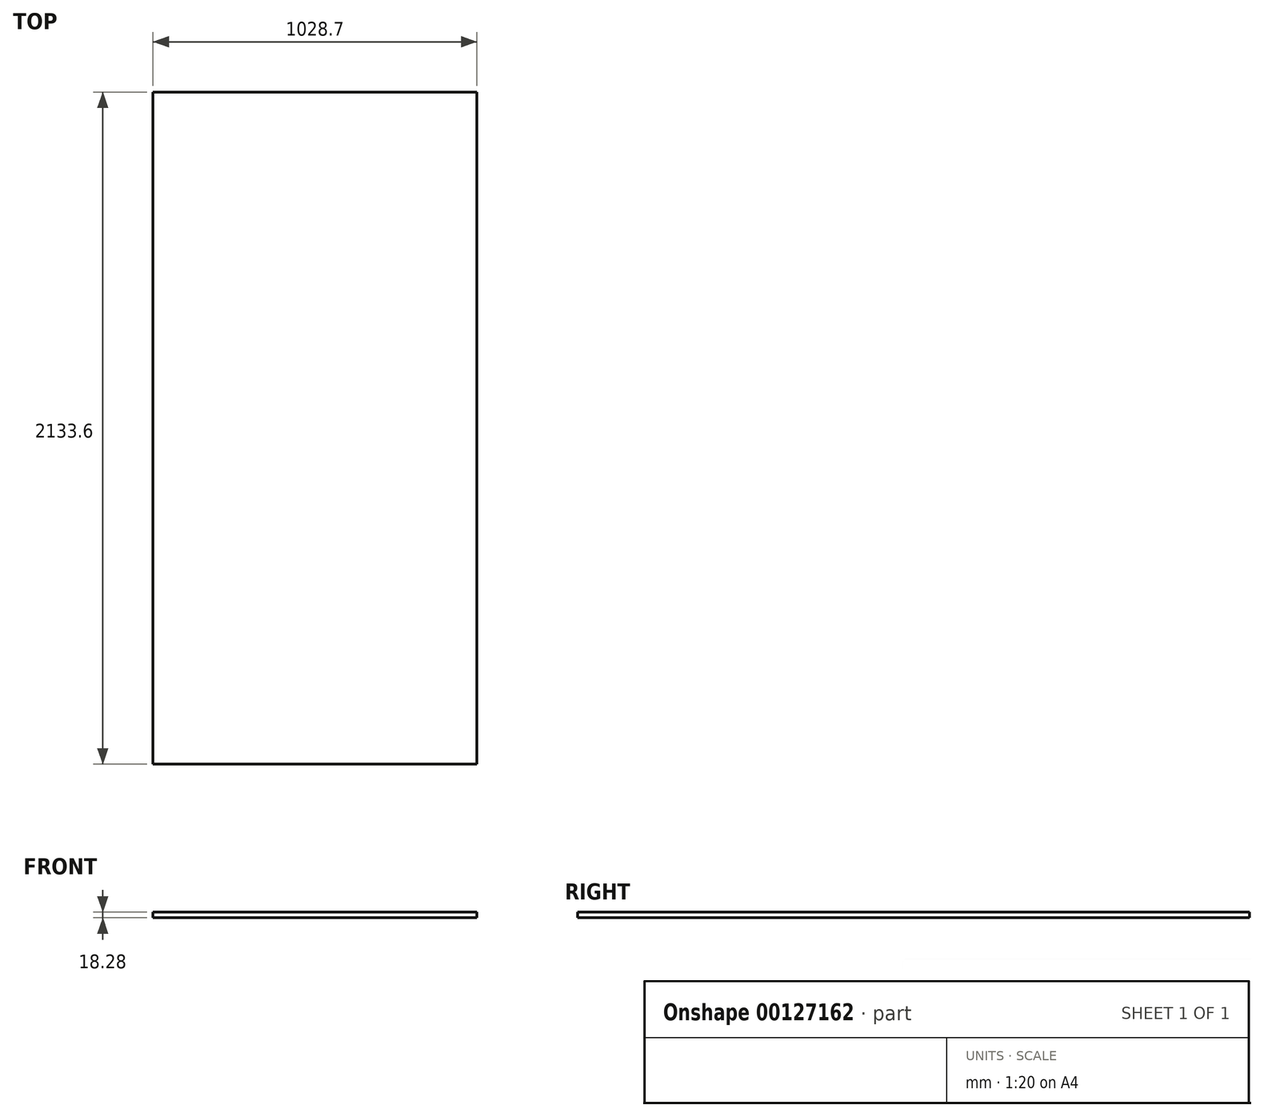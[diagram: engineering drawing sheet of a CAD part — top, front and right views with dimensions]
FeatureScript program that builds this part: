
annotation { "Feature Type Name" : "Feature", "Feature Type Description" : "" }
export const myFeature = defineFeature(function(context is Context, id is Id, definition is map)
    precondition{}
    {
        {
            var Q0;
            Q0=qCreatedBy(makeId("Front.planeOp"),FACE);
            var sketch = newSketch(context, id + "F0", { "sketchPlane" : qUnion([Q0])});
            skLineSegment(sketch, "E0.bottom", {"start": v(514.35, -9.14) * mm, "end": v(-514.35, -9.14) * mm});
            skLineSegment(sketch, "E0.top", {"start": v(514.35, 9.14) * mm, "end": v(-514.35, 9.14) * mm});
            skLineSegment(sketch, "E0.left", {"start": v(514.35, -9.14) * mm, "end": v(514.35, 9.14) * mm});
            skLineSegment(sketch, "E0.right", {"start": v(-514.35, -9.14) * mm, "end": v(-514.35, 9.14) * mm});
            skPoint(sketch, "E0.middle", {"position": v(0, 0) * mm});
            skSolve(sketch);
        }
        {
            var Q0;
            Q0=qSketchRegion(id+"F0",true);
            extrude(context, id + "F1", {"entities" : qUnion([Q0]), "depth" : 2133.6 * mm});
        }
    });
